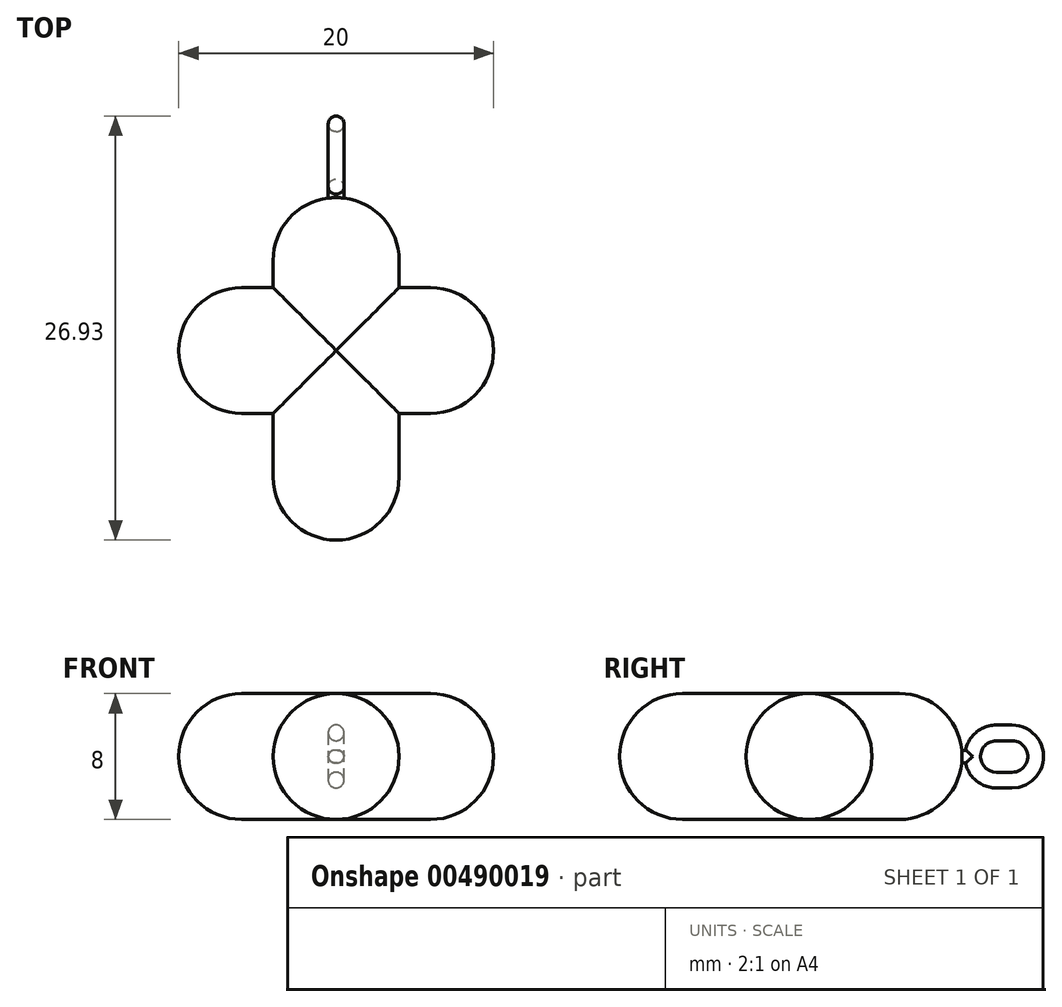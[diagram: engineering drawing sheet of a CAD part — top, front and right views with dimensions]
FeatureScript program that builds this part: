
annotation { "Feature Type Name" : "Feature", "Feature Type Description" : "" }
export const myFeature = defineFeature(function(context is Context, id is Id, definition is map)
    precondition{}
    {
        {
            var Q0;
            Q0=qCreatedBy(makeId("Top.planeOp"),FACE);
            var sketch = newSketch(context, id + "F0", { "sketchPlane" : qUnion([Q0])});
            skLineSegment(sketch, "E0.bottom", {"start": v(4, -10.88) * mm, "end": v(-4, -10.88) * mm});
            skLineSegment(sketch, "E0.top", {"start": v(4, 10.88) * mm, "end": v(-4, 10.88) * mm});
            skLineSegment(sketch, "E0.left", {"start": v(4, -10.88) * mm, "end": v(4, 10.88) * mm});
            skLineSegment(sketch, "E0.right", {"start": v(-4, -10.88) * mm, "end": v(-4, 10.88) * mm});
            skPoint(sketch, "E0.middle", {"position": v(0, 0) * mm});
            skLineSegment(sketch, "E1.bottom", {"start": v(10, 5.16) * mm, "end": v(-10, 5.16) * mm});
            skLineSegment(sketch, "E1.top", {"start": v(10, -2.84) * mm, "end": v(-10, -2.84) * mm});
            skLineSegment(sketch, "E1.left", {"start": v(10, 5.16) * mm, "end": v(10, -2.84) * mm});
            skLineSegment(sketch, "E1.right", {"start": v(-10, 5.16) * mm, "end": v(-10, -2.84) * mm});
            skPoint(sketch, "E1.middle", {"position": v(0, 1.16) * mm});
            skSolve(sketch);
        }
        {
            var Q0;
            {var subQ5=sQuery(id+"F0.wireOp",EDGE,"E1.left");Q0=makeQuery(id+"F0.imprint","IMPRINT",FACE,{"disambiguationData":[TD([[makeQuery(id+"F0.imprint","IMPRINT",EDGE,{"derivedFrom":subQ5}),-1.0]])]});}
            var Q1;
            {var subQ0=sQuery(id+"F0.wireOp",EDGE,"E1.top");var subQ1=sQuery(id+"F0.wireOp",EDGE,"E0.left");var subQ2=makeQuery(id+"F0.imprint","INTERSECT",VERTEX,{"derivedFrom":[subQ1,subQ0]});Q1=makeQuery(id+"F0.imprint","IMPRINT",FACE,{"disambiguationData":[TD([[makeQuery(id+"F0.imprint","IMPRINT",EDGE,{"disambiguationData":[TD([[subQ2,-1.0]])],"derivedFrom":subQ1}),1.0]])]});}
            var Q2;
            {var subQ0=sQuery(id+"F0.wireOp",EDGE,"E0.top");Q2=makeQuery(id+"F0.imprint","IMPRINT",FACE,{"disambiguationData":[TD([[makeQuery(id+"F0.imprint","IMPRINT",EDGE,{"derivedFrom":subQ0}),1.0]])]});}
            var Q3;
            {var subQ5=sQuery(id+"F0.wireOp",EDGE,"E1.right");Q3=makeQuery(id+"F0.imprint","IMPRINT",FACE,{"disambiguationData":[TD([[makeQuery(id+"F0.imprint","IMPRINT",EDGE,{"derivedFrom":subQ5}),1.0]])]});}
            var Q4;
            {var subQ0=sQuery(id+"F0.wireOp",EDGE,"E0.bottom");Q4=makeQuery(id+"F0.imprint","IMPRINT",FACE,{"disambiguationData":[TD([[makeQuery(id+"F0.imprint","IMPRINT",EDGE,{"derivedFrom":subQ0}),-1.0]])]});}
            extrude(context, id + "F1", {"entities" : qUnion([Q0, Q1, Q2, Q3, Q4]), "depth" : 4 * mm, "offsetDistance" : 25 * mm, "hasSecondDirection" : true, "secondDirectionOppositeDirection" : true, "secondDirectionDepth" : 4 * mm});
        }
        {
            var Q0;
            Q0=makeQuery(id+"F1.opExtrude","SWEPT_EDGE",EDGE,{"disambiguationData":[OSD([sQuery(id+"F0.wireOp",EDGE,"E0.bottom"),sQuery(id+"F0.wireOp",EDGE,"E0.left")])]});
            var Q1;
            Q1=makeQuery(id+"F1.opExtrude","SWEPT_EDGE",EDGE,{"disambiguationData":[OSD([sQuery(id+"F0.wireOp",EDGE,"E0.bottom"),sQuery(id+"F0.wireOp",EDGE,"E0.right")])]});
            var Q2;
            Q2=makeQuery(id+"F1.opExtrude","SWEPT_EDGE",EDGE,{"disambiguationData":[OSD([sQuery(id+"F0.wireOp",EDGE,"E1.top"),sQuery(id+"F0.wireOp",EDGE,"E1.right")])]});
            var Q3;
            Q3=makeQuery(id+"F1.opExtrude","SWEPT_EDGE",EDGE,{"disambiguationData":[OSD([sQuery(id+"F0.wireOp",EDGE,"E1.bottom"),sQuery(id+"F0.wireOp",EDGE,"E1.right")])]});
            var Q4;
            Q4=makeQuery(id+"F1.opExtrude","SWEPT_EDGE",EDGE,{"disambiguationData":[OSD([sQuery(id+"F0.wireOp",EDGE,"E1.top"),sQuery(id+"F0.wireOp",EDGE,"E1.left")])]});
            var Q5;
            Q5=makeQuery(id+"F1.opExtrude","SWEPT_EDGE",EDGE,{"disambiguationData":[OSD([sQuery(id+"F0.wireOp",EDGE,"E1.bottom"),sQuery(id+"F0.wireOp",EDGE,"E1.left")])]});
            var Q6;
            Q6=makeQuery(id+"F1.opExtrude","SWEPT_EDGE",EDGE,{"disambiguationData":[OSD([sQuery(id+"F0.wireOp",EDGE,"E0.top"),sQuery(id+"F0.wireOp",EDGE,"E0.left")])]});
            var Q7;
            Q7=makeQuery(id+"F1.opExtrude","SWEPT_EDGE",EDGE,{"disambiguationData":[OSD([sQuery(id+"F0.wireOp",EDGE,"E0.top"),sQuery(id+"F0.wireOp",EDGE,"E0.right")])]});
            fillet(context, id + "F2", {"entities" : qUnion([Q0, Q1, Q2, Q3, Q4, Q5, Q6, Q7]), "radius" : 4 * mm, "tangentPropagation" : true, "allowEdgeOverflow" : false});
        }
        {
            var Q0;
            {var subQ0=sQuery(id+"F0.wireOp",EDGE,"E0.left");Q0=makeQuery(id+"F1.opExtrude","CAP_EDGE",EDGE,{"disambiguationData":[OSD([subQ0]),TDD([makeQuery(id+"F0.imprint","IMPRINT",EDGE,{"disambiguationData":[TD([[makeQuery(id+"F0.imprint","INTERSECT",VERTEX,{"derivedFrom":[sQuery(id+"F0.wireOp",EDGE,"E0.bottom"),subQ0]}),-1.0]])],"derivedFrom":subQ0})])],"isStart":false});}
            var Q1;
            {var subQ0=sQuery(id+"F0.wireOp",EDGE,"E0.right");Q1=makeQuery(id+"F1.opExtrude","CAP_EDGE",EDGE,{"disambiguationData":[OSD([subQ0]),TDD([makeQuery(id+"F0.imprint","IMPRINT",EDGE,{"disambiguationData":[TD([[makeQuery(id+"F0.imprint","INTERSECT",VERTEX,{"derivedFrom":[sQuery(id+"F0.wireOp",EDGE,"E0.bottom"),subQ0]}),-1.0]])],"derivedFrom":subQ0})])],"isStart":false});}
            var Q2;
            {var subQ0=sQuery(id+"F0.wireOp",EDGE,"E1.bottom");Q2=makeQuery(id+"F1.opExtrude","CAP_EDGE",EDGE,{"disambiguationData":[OSD([subQ0]),TDD([makeQuery(id+"F0.imprint","IMPRINT",EDGE,{"disambiguationData":[TD([[makeQuery(id+"F0.imprint","INTERSECT",VERTEX,{"derivedFrom":[subQ0,sQuery(id+"F0.wireOp",EDGE,"E1.left")]}),-1.0]])],"derivedFrom":subQ0})])],"isStart":false});}
            var Q3;
            {var subQ0=sQuery(id+"F0.wireOp",EDGE,"E0.right");Q3=makeQuery(id+"F1.opExtrude","CAP_EDGE",EDGE,{"disambiguationData":[OSD([subQ0]),TDD([makeQuery(id+"F0.imprint","IMPRINT",EDGE,{"disambiguationData":[TD([[makeQuery(id+"F0.imprint","INTERSECT",VERTEX,{"derivedFrom":[sQuery(id+"F0.wireOp",EDGE,"E0.top"),subQ0]}),1.0]])],"derivedFrom":subQ0})])],"isStart":false});}
            var Q4;
            {var subQ0=sQuery(id+"F0.wireOp",EDGE,"E1.bottom");Q4=makeQuery(id+"F1.opExtrude","CAP_EDGE",EDGE,{"disambiguationData":[OSD([subQ0]),TDD([makeQuery(id+"F0.imprint","IMPRINT",EDGE,{"disambiguationData":[TD([[makeQuery(id+"F0.imprint","INTERSECT",VERTEX,{"derivedFrom":[subQ0,sQuery(id+"F0.wireOp",EDGE,"E1.right")]}),1.0]])],"derivedFrom":subQ0})])],"isStart":false});}
            var Q5;
            {var subQ0=sQuery(id+"F0.wireOp",EDGE,"E1.top");Q5=makeQuery(id+"F1.opExtrude","CAP_EDGE",EDGE,{"disambiguationData":[OSD([subQ0]),TDD([makeQuery(id+"F0.imprint","IMPRINT",EDGE,{"disambiguationData":[TD([[makeQuery(id+"F0.imprint","INTERSECT",VERTEX,{"derivedFrom":[subQ0,sQuery(id+"F0.wireOp",EDGE,"E1.right")]}),1.0]])],"derivedFrom":subQ0})])],"isStart":false});}
            var Q6;
            {var subQ0=sQuery(id+"F0.wireOp",EDGE,"E1.top");Q6=makeQuery(id+"F1.opExtrude","CAP_EDGE",EDGE,{"disambiguationData":[OSD([subQ0]),TDD([makeQuery(id+"F0.imprint","IMPRINT",EDGE,{"disambiguationData":[TD([[makeQuery(id+"F0.imprint","INTERSECT",VERTEX,{"derivedFrom":[subQ0,sQuery(id+"F0.wireOp",EDGE,"E1.left")]}),-1.0]])],"derivedFrom":subQ0})])],"isStart":false});}
            var Q7;
            {var subQ0=sQuery(id+"F0.wireOp",EDGE,"E0.left");Q7=makeQuery(id+"F1.opExtrude","CAP_EDGE",EDGE,{"disambiguationData":[OSD([subQ0]),TDD([makeQuery(id+"F0.imprint","IMPRINT",EDGE,{"disambiguationData":[TD([[makeQuery(id+"F0.imprint","INTERSECT",VERTEX,{"derivedFrom":[sQuery(id+"F0.wireOp",EDGE,"E0.top"),subQ0]}),1.0]])],"derivedFrom":subQ0})])],"isStart":true});}
            var Q8;
            {var subQ0=sQuery(id+"F0.wireOp",EDGE,"E1.bottom");Q8=makeQuery(id+"F1.opExtrude","CAP_EDGE",EDGE,{"disambiguationData":[OSD([subQ0]),TDD([makeQuery(id+"F0.imprint","IMPRINT",EDGE,{"disambiguationData":[TD([[makeQuery(id+"F0.imprint","INTERSECT",VERTEX,{"derivedFrom":[subQ0,sQuery(id+"F0.wireOp",EDGE,"E1.left")]}),-1.0]])],"derivedFrom":subQ0})])],"isStart":true});}
            var Q9;
            {var subQ0=sQuery(id+"F0.wireOp",EDGE,"E1.bottom");Q9=makeQuery(id+"F1.opExtrude","CAP_EDGE",EDGE,{"disambiguationData":[OSD([subQ0]),TDD([makeQuery(id+"F0.imprint","IMPRINT",EDGE,{"disambiguationData":[TD([[makeQuery(id+"F0.imprint","INTERSECT",VERTEX,{"derivedFrom":[subQ0,sQuery(id+"F0.wireOp",EDGE,"E1.right")]}),1.0]])],"derivedFrom":subQ0})])],"isStart":true});}
            var Q10;
            {var subQ0=sQuery(id+"F0.wireOp",EDGE,"E0.right");Q10=makeQuery(id+"F1.opExtrude","CAP_EDGE",EDGE,{"disambiguationData":[OSD([subQ0]),TDD([makeQuery(id+"F0.imprint","IMPRINT",EDGE,{"disambiguationData":[TD([[makeQuery(id+"F0.imprint","INTERSECT",VERTEX,{"derivedFrom":[sQuery(id+"F0.wireOp",EDGE,"E0.bottom"),subQ0]}),-1.0]])],"derivedFrom":subQ0})])],"isStart":true});}
            fillet(context, id + "F3", {"entities" : qUnion([Q0, Q1, Q2, Q3, Q4, Q5, Q6, Q7, Q8, Q9, Q10]), "radius" : 4 * mm, "tangentPropagation" : true, "allowEdgeOverflow" : false});
        }
        {
            var Q0;
            Q0=qCreatedBy(makeId("Right.planeOp"),FACE);
            var sketch = newSketch(context, id + "F4", { "sketchPlane" : qUnion([Q0])});
            skLineSegment(sketch, "E2.bottom", {"start": v(13.05, -1) * mm, "end": v(14.05, -1) * mm});
            skLineSegment(sketch, "E2.top", {"start": v(13.05, 1) * mm, "end": v(14.05, 1) * mm});
            skLineSegment(sketch, "E2.left", {"start": v(12.05, 0) * mm, "end": v(12.05, 0) * mm});
            skLineSegment(sketch, "E2.right", {"start": v(15.05, 0) * mm, "end": v(15.05, 0) * mm});
            skPoint(sketch, "E2.middle", {"position": v(13.55, 0) * mm});
            skLineSegment(sketch, "E3.0", {"start": v(16.05, 0) * mm, "end": v(16.05, 0) * mm});
            skLineSegment(sketch, "E3.1", {"start": v(13.05, -2) * mm, "end": v(14.05, -2) * mm});
            skLineSegment(sketch, "E3.2", {"start": v(11.05, 0) * mm, "end": v(11.05, 0) * mm});
            skLineSegment(sketch, "E3.3", {"start": v(13.05, 2) * mm, "end": v(14.05, 2) * mm});
            skPoint(sketch, "E4.visualSharp", {"position": v(15.05, -1) * mm});
            skArc(sketch, "E4.filletArc", {"start": v(14.05, -1) * mm, "mid": v(14.76, -0.7) * mm, "end": v(15.05, 0) * mm});
            skPoint(sketch, "E5.visualSharp", {"position": v(12.05, -1) * mm});
            skArc(sketch, "E5.filletArc", {"start": v(12.05, 0) * mm, "mid": v(12.34, -0.7) * mm, "end": v(13.05, -1) * mm});
            skPoint(sketch, "E6.visualSharp", {"position": v(12.05, 1) * mm});
            skArc(sketch, "E6.filletArc", {"start": v(13.05, 1) * mm, "mid": v(12.34, 0.7) * mm, "end": v(12.05, 0) * mm});
            skPoint(sketch, "E7.visualSharp", {"position": v(15.05, 1) * mm});
            skArc(sketch, "E7.filletArc", {"start": v(15.05, 0) * mm, "mid": v(14.76, 0.7) * mm, "end": v(14.05, 1) * mm});
            skPoint(sketch, "E8.visualSharp", {"position": v(16.05, -2) * mm});
            skArc(sketch, "E8.filletArc", {"start": v(14.05, -2) * mm, "mid": v(15.46, -1.41) * mm, "end": v(16.05, 0) * mm});
            skPoint(sketch, "E9.visualSharp", {"position": v(11.05, -2) * mm});
            skArc(sketch, "E9.filletArc", {"start": v(11.05, 0) * mm, "mid": v(11.64, -1.41) * mm, "end": v(13.05, -2) * mm});
            skPoint(sketch, "E10.visualSharp", {"position": v(11.05, 2) * mm});
            skArc(sketch, "E10.filletArc", {"start": v(13.05, 2) * mm, "mid": v(11.64, 1.41) * mm, "end": v(11.05, 0) * mm});
            skPoint(sketch, "E11.visualSharp", {"position": v(16.05, 2) * mm});
            skArc(sketch, "E11.filletArc", {"start": v(16.05, 0) * mm, "mid": v(15.46, 1.41) * mm, "end": v(14.05, 2) * mm});
            skLineSegment(sketch, "E12.bottom", {"start": v(10.78, -0.4) * mm, "end": v(11.43, -0.4) * mm});
            skLineSegment(sketch, "E12.top", {"start": v(10.78, 0.4) * mm, "end": v(11.43, 0.4) * mm});
            skLineSegment(sketch, "E12.left", {"start": v(10.78, -0.4) * mm, "end": v(10.78, 0.4) * mm});
            skLineSegment(sketch, "E12.right", {"start": v(11.43, -0.4) * mm, "end": v(11.43, 0.4) * mm});
            skPoint(sketch, "E12.middle", {"position": v(11.1, 0) * mm});
            skSolve(sketch);
        }
        {
            var Q0;
            Q0=makeQuery(id+"F4.imprint","IMPRINT",FACE,{"disambiguationData":[TD([[makeQuery(id+"F4.imprint","IMPRINT",EDGE,{"derivedFrom":sQuery(id+"F4.wireOp",EDGE,"E2.bottom")}),-1.0]])]});
            var Q1;
            {var subQ0=sQuery(id+"F4.wireOp",EDGE,"E12.right");Q1=makeQuery(id+"F4.imprint","IMPRINT",FACE,{"disambiguationData":[TD([[makeQuery(id+"F4.imprint","IMPRINT",EDGE,{"derivedFrom":subQ0}),1.0]])]});}
            var Q2;
            {var subQ0=sQuery(id+"F4.wireOp",EDGE,"E12.left");Q2=makeQuery(id+"F4.imprint","IMPRINT",FACE,{"disambiguationData":[TD([[makeQuery(id+"F4.imprint","IMPRINT",EDGE,{"derivedFrom":subQ0}),-1.0]])]});}
            extrude(context, id + "F5", {"entities" : qUnion([Q0, Q1, Q2]), "operationType" : NewBodyOperationType.ADD, "depth" : .5 * mm, "offsetDistance" : 25 * mm, "hasSecondDirection" : true, "secondDirectionOppositeDirection" : true, "secondDirectionDepth" : .5 * mm});
        }
        {
            var Q0;
            Q0=makeQuery(id+"F5.opExtrude","CAP_EDGE",EDGE,{"disambiguationData":[OSD([sQuery(id+"F4.wireOp",EDGE,"E2.top")])],"isStart":false});
            var Q1;
            Q1=makeQuery(id+"F5.opExtrude","CAP_EDGE",EDGE,{"disambiguationData":[OSD([sQuery(id+"F4.wireOp",EDGE,"E8.filletArc"),sQuery(id+"F4.wireOp",EDGE,"E11.filletArc")])],"isStart":false});
            var Q2;
            Q2=makeQuery(id+"F5.opExtrude","CAP_EDGE",EDGE,{"disambiguationData":[OSD([sQuery(id+"F4.wireOp",EDGE,"E8.filletArc"),sQuery(id+"F4.wireOp",EDGE,"E11.filletArc")])],"isStart":true});
            var Q3;
            Q3=makeQuery(id+"F5.opExtrude","CAP_EDGE",EDGE,{"disambiguationData":[OSD([sQuery(id+"F4.wireOp",EDGE,"E5.filletArc"),sQuery(id+"F4.wireOp",EDGE,"E6.filletArc")])],"isStart":true});
            fillet(context, id + "F6", {"entities" : qUnion([Q0, Q1, Q2, Q3]), "radius" : .5 * mm, "tangentPropagation" : true, "allowEdgeOverflow" : false});
        }
        {
            var Q0;
            Q0=makeQuery(id+"F5.opExtrude","CAP_EDGE",EDGE,{"disambiguationData":[OSD([sQuery(id+"F4.wireOp",EDGE,"E12.bottom")])],"isStart":true});
            var Q1;
            Q1=makeQuery(id+"F5.opExtrude","CAP_EDGE",EDGE,{"disambiguationData":[OSD([sQuery(id+"F4.wireOp",EDGE,"E12.top")])],"isStart":true});
            var Q2;
            Q2=makeQuery(id+"F5.opExtrude","CAP_EDGE",EDGE,{"disambiguationData":[OSD([sQuery(id+"F4.wireOp",EDGE,"E12.bottom")])],"isStart":false});
            var Q3;
            Q3=makeQuery(id+"F5.opExtrude","CAP_EDGE",EDGE,{"disambiguationData":[OSD([sQuery(id+"F4.wireOp",EDGE,"E12.top")])],"isStart":false});
            fillet(context, id + "F7", {"entities" : qUnion([Q0, Q1, Q2, Q3]), "radius" : .4 * mm, "tangentPropagation" : true, "allowEdgeOverflow" : false});
        }
    });
